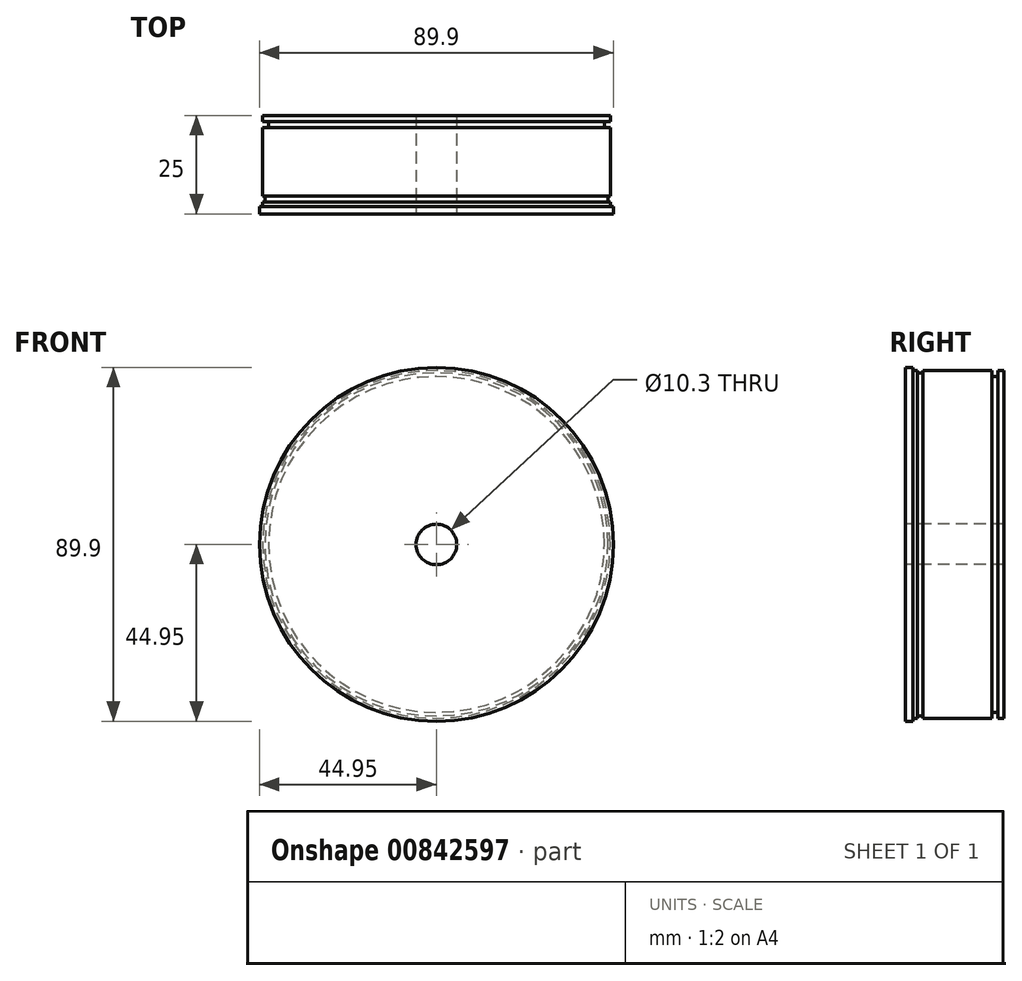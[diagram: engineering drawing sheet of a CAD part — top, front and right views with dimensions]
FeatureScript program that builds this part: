
annotation { "Feature Type Name" : "Feature", "Feature Type Description" : "" }
export const myFeature = defineFeature(function(context is Context, id is Id, definition is map)
    precondition{}
    {
        {
            var Q0;
            Q0=qCreatedBy(makeId("Top.planeOp"),FACE);
            var sketch = newSketch(context, id + "F0", { "sketchPlane" : qUnion([Q0])});
            skLineSegment(sketch, "E0.bottom", {"start": v(0, 0) * mm, "end": v(44.95, 0) * mm});
            skLineSegment(sketch, "E0.top", {"start": v(0, 25) * mm, "end": v(44.16, 25) * mm});
            skLineSegment(sketch, "E0.left", {"start": v(0, 0) * mm, "end": v(0, 25) * mm});
            skLineSegment(sketch, "E0.right", {"start": v(44.95, 0) * mm, "end": v(44.95, 1.87) * mm});
            skLineSegment(sketch, "E1.top", {"start": v(44.95, 1.87) * mm, "end": v(44.16, 1.87) * mm});
            skLineSegment(sketch, "E1.right", {"start": v(44.16, 25) * mm, "end": v(44.16, 23.5) * mm});
            skLineSegment(sketch, "E2.bottom", {"start": v(44.16, 3) * mm, "end": v(43.59, 3) * mm});
            skLineSegment(sketch, "E2.top", {"start": v(44.16, 4.5) * mm, "end": v(43.59, 4.5) * mm});
            skLineSegment(sketch, "E2.right", {"start": v(43.59, 3) * mm, "end": v(43.59, 4.5) * mm});
            skLineSegment(sketch, "E3.trimOffspring", {"start": v(44.16, 3) * mm, "end": v(44.16, 1.87) * mm});
            skLineSegment(sketch, "E4.bottom", {"start": v(44.16, 23.5) * mm, "end": v(42.66, 23.5) * mm});
            skLineSegment(sketch, "E4.top", {"start": v(44.16, 22) * mm, "end": v(42.66, 22) * mm});
            skLineSegment(sketch, "E4.right", {"start": v(42.66, 23.5) * mm, "end": v(42.66, 22) * mm});
            skLineSegment(sketch, "E5.trimOffspring", {"start": v(44.16, 22) * mm, "end": v(44.16, 4.5) * mm});
            skSolve(sketch);
        }
        {
            var Q0;
            Q0 = qSketchRegion(id + "F0", true);
            var Q1;
            Q1=sQuery(id+"F0.wireOp",EDGE,"E0.left");
            revolve(context, id + "F1", {"surfaceOperationType" : NewSurfaceOperationType.NEW, "entities" : qUnion([Q0]), "axis" : qUnion([Q1]), "revolveType" : RevolveType.FULL});
        }
        {
            var Q0;
            Q0=qCreatedBy(makeId("Front.planeOp"),FACE);
            var sketch = newSketch(context, id + "F2", { "sketchPlane" : qUnion([Q0])});
            skPoint(sketch, "E6", {"position": v(0, 0) * mm});
            skSolve(sketch);
        }
        {
            var Q0;
            Q0=sQuery(id+"F2.wireOp",VERTEX,"E6");
            var Q1;
            Q1=makeQuery(id+"F1.opRevolve","SWEPT_BODY",BODY,{"disambiguationData":[OSD([sQuery(id+"F0.wireOp",EDGE,"E0.bottom"),sQuery(id+"F0.wireOp",EDGE,"E0.top"),sQuery(id+"F0.wireOp",EDGE,"E0.left"),sQuery(id+"F0.wireOp",EDGE,"E0.right"),sQuery(id+"F0.wireOp",EDGE,"E1.top"),sQuery(id+"F0.wireOp",EDGE,"E1.right"),sQuery(id+"F0.wireOp",EDGE,"E2.bottom"),sQuery(id+"F0.wireOp",EDGE,"E2.top"),sQuery(id+"F0.wireOp",EDGE,"E2.right"),sQuery(id+"F0.wireOp",EDGE,"E3.trimOffspring"),sQuery(id+"F0.wireOp",EDGE,"E4.bottom"),sQuery(id+"F0.wireOp",EDGE,"E4.top"),sQuery(id+"F0.wireOp",EDGE,"E4.right"),sQuery(id+"F0.wireOp",EDGE,"E5.trimOffspring")])]});
            hole(context, id + "F3", {"style" : HoleStyle.SIMPLE, "endStyle" : HoleEndStyle.THROUGH, "standardTappedOrClearance" : lookupTablePath({ "standard" : "ISO", "engagement" : "75%", "pitch" : "1.75 mm", "size" : "M12", "type" : "Tapped" }), "standardBlindInLast" : lookupTablePath({ "standard" : "ISO", "engagement" : "75%", "pitch" : "1.75 mm", "size" : "M12", "type" : "Tapped" }), "holeDiameter" : 10.3 * mm, "majorDiameter" : 12 * mm, "showTappedDepth" : true, "isTappedThrough" : true, "tappedDepth" : 6 * mm, "tapClearance" : 3, "locations" : qUnion([Q0]), "scope" : qUnion([Q1])});
        }
    });
